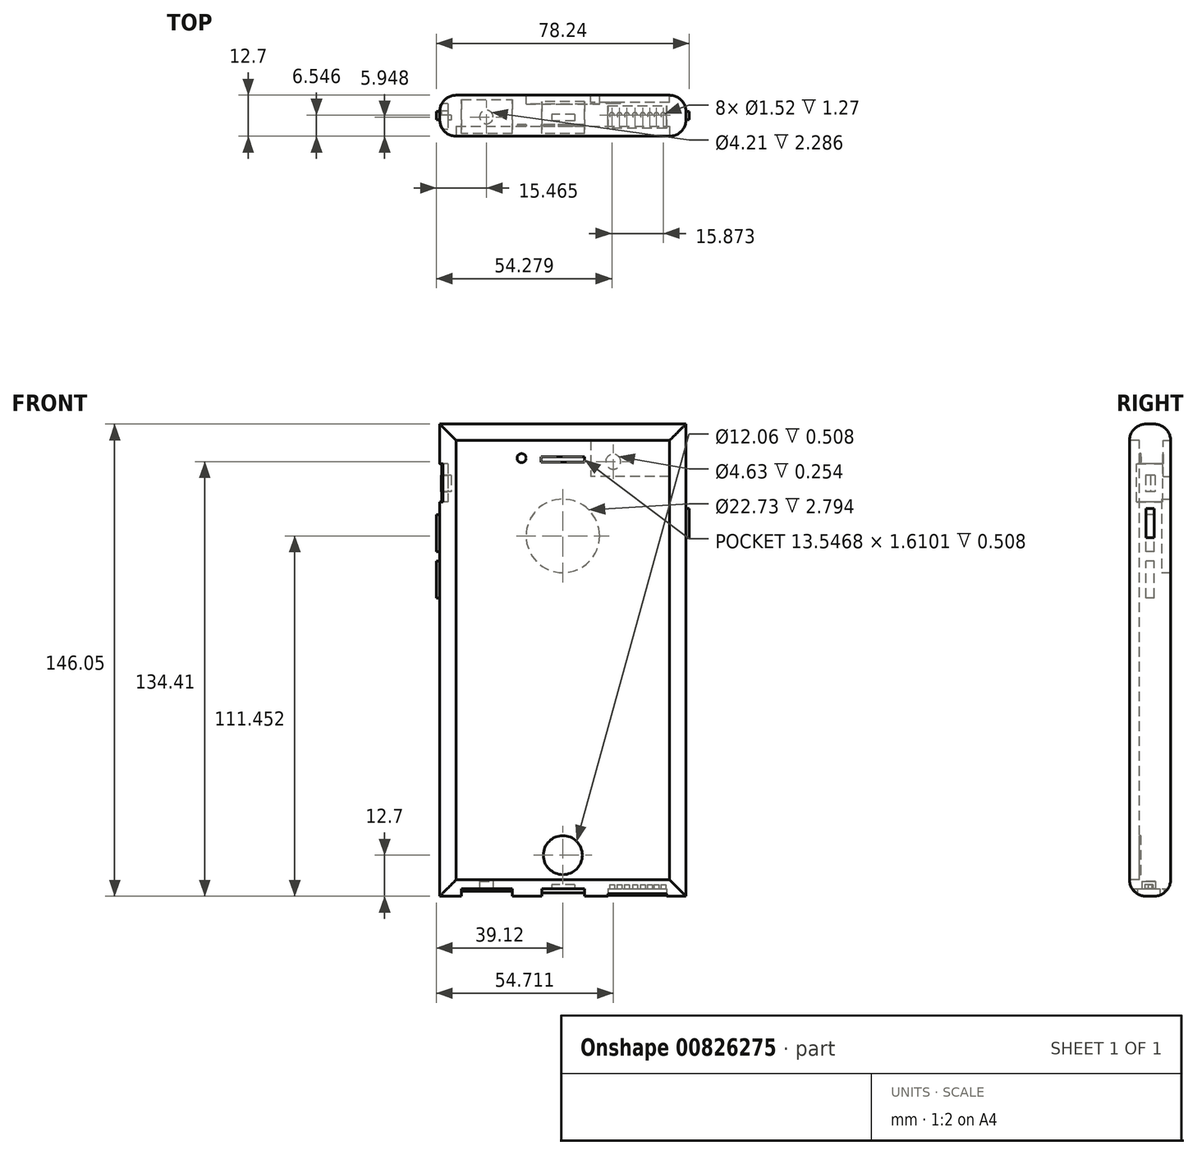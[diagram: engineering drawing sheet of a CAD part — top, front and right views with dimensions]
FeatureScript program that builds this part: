
annotation { "Feature Type Name" : "Feature", "Feature Type Description" : "" }
export const myFeature = defineFeature(function(context is Context, id is Id, definition is map)
    precondition{}
    {
        {
            var Q0;
            Q0=qCreatedBy(makeId("Front.planeOp"),FACE);
            var sketch = newSketch(context, id + "F0", { "sketchPlane" : qUnion([Q0])});
            skLineSegment(sketch, "E0.bottom", {"start": v(0, 0) * mm, "end": v(76.2, 0) * mm});
            skLineSegment(sketch, "E0.top", {"start": v(0, 146.05) * mm, "end": v(76.2, 146.05) * mm});
            skLineSegment(sketch, "E0.left", {"start": v(0, 0) * mm, "end": v(0, 146.05) * mm});
            skLineSegment(sketch, "E0.right", {"start": v(76.2, 0) * mm, "end": v(76.2, 146.05) * mm});
            skSolve(sketch);
        }
        {
            var Q0;
            Q0=makeQuery(id+"F0.imprint","IMPRINT",FACE,{"disambiguationData":[TD([[makeQuery(id+"F0.imprint","IMPRINT",EDGE,{"derivedFrom":sQuery(id+"F0.wireOp",EDGE,"E0.bottom")}),1.0]])]});
            extrude(context, id + "F1", {"entities" : qUnion([Q0]), "depth" : 12.7 * mm, "offsetDistance" : 25.4 * mm});
        }
        {
            var Q0;
            Q0=makeQuery(id+"F1.opExtrude","CAP_FACE",FACE,{"disambiguationData":[OSD([sQuery(id+"F0.wireOp",EDGE,"E0.bottom"),sQuery(id+"F0.wireOp",EDGE,"E0.top"),sQuery(id+"F0.wireOp",EDGE,"E0.left"),sQuery(id+"F0.wireOp",EDGE,"E0.right")])],"isStart":false});
            fillet(context, id + "F2", {"entities" : qUnion([Q0]), "radius" : 5.08 * mm, "tangentPropagation" : true, "allowEdgeOverflow" : false});
        }
        {
            var Q0;
            Q0=makeQuery(id+"F1.opExtrude","CAP_FACE",FACE,{"disambiguationData":[OSD([sQuery(id+"F0.wireOp",EDGE,"E0.bottom"),sQuery(id+"F0.wireOp",EDGE,"E0.top"),sQuery(id+"F0.wireOp",EDGE,"E0.left"),sQuery(id+"F0.wireOp",EDGE,"E0.right")])],"isStart":true});
            fillet(context, id + "F3", {"entities" : qUnion([Q0]), "radius" : 5.08 * mm, "tangentPropagation" : true, "allowEdgeOverflow" : false});
        }
        {
            var Q0;
            Q0=makeQuery(id+"F1.opExtrude","CAP_FACE",FACE,{"disambiguationData":[OSD([sQuery(id+"F0.wireOp",EDGE,"E0.bottom"),sQuery(id+"F0.wireOp",EDGE,"E0.top"),sQuery(id+"F0.wireOp",EDGE,"E0.left"),sQuery(id+"F0.wireOp",EDGE,"E0.right")])],"isStart":false});
            extrude(context, id + "F4", {"entities" : qUnion([Q0]), "operationType" : NewBodyOperationType.REMOVE, "oppositeDirection" : true, "depth" : 2.54 * mm, "offsetDistance" : 25.4 * mm});
        }
        {
            var Q0;
            Q0=makeQuery(id+"F1.opExtrude","SWEPT_FACE",FACE,{"disambiguationData":[OSD([sQuery(id+"F0.wireOp",EDGE,"E0.left")])]});
            var sketch = newSketch(context, id + "F5", { "sketchPlane" : qUnion([Q0])});
            skLineSegment(sketch, "E1.bottom", {"start": v(2.58, 133.75) * mm, "end": v(10.56, 133.75) * mm});
            skLineSegment(sketch, "E1.top", {"start": v(2.58, 122) * mm, "end": v(10.56, 122) * mm});
            skLineSegment(sketch, "E1.left", {"start": v(2.58, 133.75) * mm, "end": v(2.58, 122) * mm});
            skLineSegment(sketch, "E1.right", {"start": v(10.56, 133.75) * mm, "end": v(10.56, 122) * mm});
            skSolve(sketch);
        }
        {
            var Q0;
            {var subQ0=sQuery(id+"F5.wireOp",EDGE,"E1.left");Q0=makeQuery(id+"F5.imprint","IMPRINT",FACE,{"disambiguationData":[TD([[makeQuery(id+"F5.imprint","IMPRINT",EDGE,{"derivedFrom":subQ0}),1.0]])]});}
            var Q1;
            {var subQ0=sQuery(id+"F5.wireOp",EDGE,"E1.bottom");var subQ1=sQuery(id+"F0.wireOp",EDGE,"E0.left");var subQ2=makeQuery(id+"F1.opExtrude","SWEPT_FACE",FACE,{"disambiguationData":[OSD([subQ1])]});var subQ3=makeQuery(id+"F3.opFillet","BLEND_EDGE",EDGE,{"blendedFrom":[makeQuery(id+"F1.opExtrude","CAP_EDGE",EDGE,{"disambiguationData":[OSD([subQ1])],"isStart":true}),subQ2],"blendedInto":[subQ2]});var subQ4=makeQuery(id+"F5.imprint","INTERSECT",VERTEX,{"derivedFrom":[subQ3,subQ0]});Q1=makeQuery(id+"F5.imprint","IMPRINT",FACE,{"disambiguationData":[TD([[makeQuery(id+"F5.imprint","IMPRINT",EDGE,{"disambiguationData":[TD([[subQ4,-1.0]])],"derivedFrom":subQ0}),-1.0]])]});}
            var Q2;
            {var subQ0=sQuery(id+"F5.wireOp",EDGE,"E1.right");Q2=makeQuery(id+"F5.imprint","IMPRINT",FACE,{"disambiguationData":[TD([[makeQuery(id+"F5.imprint","IMPRINT",EDGE,{"derivedFrom":subQ0}),-1.0]])]});}
            extrude(context, id + "F6", {"entities" : qUnion([Q0, Q1, Q2]), "operationType" : NewBodyOperationType.REMOVE, "oppositeDirection" : true, "depth" : 2.54 * mm, "offsetDistance" : 25.4 * mm});
        }
        {
            var Q0;
            Q0=makeQuery(id+"F6.boolean.opBoolean","COPY",FACE,{"derivedFrom":makeQuery(id+"F6.opExtrude","CAP_FACE",FACE,{"disambiguationData":[OSD([sQuery(id+"F5.wireOp",EDGE,"E1.bottom"),sQuery(id+"F5.wireOp",EDGE,"E1.top"),sQuery(id+"F5.wireOp",EDGE,"E1.left"),sQuery(id+"F5.wireOp",EDGE,"E1.right")])],"isStart":false})});
            var sketch = newSketch(context, id + "F7", { "sketchPlane" : qUnion([Q0])});
            skLineSegment(sketch, "E2.bottom", {"start": v(4.8, 130.2) * mm, "end": v(7.68, 130.2) * mm});
            skLineSegment(sketch, "E2.top", {"start": v(4.8, 125.1) * mm, "end": v(7.68, 125.1) * mm});
            skLineSegment(sketch, "E2.left", {"start": v(4.8, 130.2) * mm, "end": v(4.8, 125.1) * mm});
            skLineSegment(sketch, "E2.right", {"start": v(7.68, 130.2) * mm, "end": v(7.68, 125.1) * mm});
            skSolve(sketch);
        }
        {
            var Q0;
            Q0=qSketchRegion(id+"F7",true);
            extrude(context, id + "F8", {"entities" : qUnion([Q0]), "operationType" : NewBodyOperationType.ADD, "depth" : 2.03 * mm, "offsetDistance" : 25.4 * mm});
        }
        {
            var Q0;
            Q0=makeQuery(id+"F8.opExtrude","CAP_FACE",FACE,{"disambiguationData":[OSD([sQuery(id+"F7.wireOp",EDGE,"E2.bottom"),sQuery(id+"F7.wireOp",EDGE,"E2.top"),sQuery(id+"F7.wireOp",EDGE,"E2.left"),sQuery(id+"F7.wireOp",EDGE,"E2.right")])],"isStart":false});
            var sketch = newSketch(context, id + "F9", { "sketchPlane" : qUnion([Q0])});
            skLineSegment(sketch, "E3", {"start": v(7.68, 125.1) * mm, "end": v(7.68, 130.2) * mm});
            skLineSegment(sketch, "E4", {"start": v(7.68, 130.2) * mm, "end": v(6.24, 130.2) * mm});
            skLineSegment(sketch, "E5", {"start": v(6.24, 130.2) * mm, "end": v(6.24, 125.1) * mm});
            skLineSegment(sketch, "E6", {"start": v(6.24, 125.1) * mm, "end": v(7.68, 125.1) * mm});
            skSolve(sketch);
        }
        {
            var Q0;
            Q0=makeQuery(id+"F9.imprint","IMPRINT",FACE,{"disambiguationData":[TD([[makeQuery(id+"F9.imprint","IMPRINT",EDGE,{"derivedFrom":sQuery(id+"F9.wireOp",EDGE,"E3")}),-1.0]])]});
            extrude(context, id + "F10", {"entities" : qUnion([Q0]), "operationType" : NewBodyOperationType.REMOVE, "oppositeDirection" : true, "depth" : 3.05 * mm, "offsetDistance" : 25.4 * mm});
        }
        {
            var Q0;
            {var subQ0=sQuery(id+"F0.wireOp",EDGE,"E0.bottom");var subQ1=sQuery(id+"F0.wireOp",EDGE,"E0.left");Q0=makeQuery(id+"F6.boolean.opBoolean","SPLIT",FACE,{"disambiguationData":[TD([makeQuery(id+"F1.opExtrude","SWEPT_FACE",FACE,{"disambiguationData":[OSD([subQ0])]})])],"derivedFrom":makeQuery(id+"F1.opExtrude","SWEPT_FACE",FACE,{"disambiguationData":[OSD([subQ1])]})});}
            var sketch = newSketch(context, id + "F11", { "sketchPlane" : qUnion([Q0])});
            skLineSegment(sketch, "E7.bottom", {"start": v(5.08, 118.03) * mm, "end": v(7.62, 118.03) * mm});
            skLineSegment(sketch, "E7.top", {"start": v(5.08, 106.6) * mm, "end": v(7.62, 106.6) * mm});
            skLineSegment(sketch, "E7.left", {"start": v(5.08, 118.03) * mm, "end": v(5.08, 106.6) * mm});
            skLineSegment(sketch, "E7.right", {"start": v(7.62, 118.03) * mm, "end": v(7.62, 106.6) * mm});
            skSolve(sketch);
        }
        {
            var Q0;
            Q0=makeQuery(id+"F11.imprint","IMPRINT",FACE,{"disambiguationData":[TD([[makeQuery(id+"F11.imprint","IMPRINT",EDGE,{"derivedFrom":sQuery(id+"F11.wireOp",EDGE,"E7.bottom")}),-1.0]])]});
            extrude(context, id + "F12", {"entities" : qUnion([Q0]), "operationType" : NewBodyOperationType.ADD, "depth" : 1.02 * mm, "offsetDistance" : 25.4 * mm});
        }
        {
            var Q0;
            {var subQ0=sQuery(id+"F0.wireOp",EDGE,"E0.bottom");var subQ2=sQuery(id+"F0.wireOp",EDGE,"E0.left");var subQ5=makeQuery(id+"F1.opExtrude","SWEPT_FACE",FACE,{"disambiguationData":[OSD([subQ0])]});Q0=makeQuery(id+"F12.boolean.opBoolean","SPLIT",FACE,{"disambiguationData":[TD([subQ5])],"derivedFrom":makeQuery(id+"F6.boolean.opBoolean","SPLIT",FACE,{"disambiguationData":[TD([subQ5])],"derivedFrom":makeQuery(id+"F1.opExtrude","SWEPT_FACE",FACE,{"disambiguationData":[OSD([subQ2])]})})});}
            var sketch = newSketch(context, id + "F13", { "sketchPlane" : qUnion([Q0])});
            skLineSegment(sketch, "E8.bottom", {"start": v(5.08, 103.7) * mm, "end": v(7.62, 103.7) * mm});
            skLineSegment(sketch, "E8.top", {"start": v(5.08, 92.27) * mm, "end": v(7.62, 92.27) * mm});
            skLineSegment(sketch, "E8.left", {"start": v(5.08, 103.7) * mm, "end": v(5.08, 92.27) * mm});
            skLineSegment(sketch, "E8.right", {"start": v(7.62, 103.7) * mm, "end": v(7.62, 92.27) * mm});
            skSolve(sketch);
        }
        {
            var Q0;
            Q0=makeQuery(id+"F13.imprint","IMPRINT",FACE,{"disambiguationData":[TD([[makeQuery(id+"F13.imprint","IMPRINT",EDGE,{"derivedFrom":sQuery(id+"F13.wireOp",EDGE,"E8.bottom")}),-1.0]])]});
            extrude(context, id + "F14", {"entities" : qUnion([Q0]), "operationType" : NewBodyOperationType.ADD, "depth" : 1.02 * mm, "offsetDistance" : 25.4 * mm});
        }
        {
            var Q0;
            Q0=makeQuery(id+"F4.boolean.opBoolean","COPY",FACE,{"derivedFrom":makeQuery(id+"F4.opExtrude","CAP_FACE",FACE,{"disambiguationData":[OSD([sQuery(id+"F0.wireOp",EDGE,"E0.bottom"),sQuery(id+"F0.wireOp",EDGE,"E0.top"),sQuery(id+"F0.wireOp",EDGE,"E0.left"),sQuery(id+"F0.wireOp",EDGE,"E0.right")])],"isStart":false})});
            var sketch = newSketch(context, id + "F15", { "sketchPlane" : qUnion([Q0])});
            skLineSegment(sketch, "E9", {"start": v(5.08, 5.08) * mm, "end": v(38.1, 5.08) * mm});
            skLineSegment(sketch, "E10", {"start": v(38.1, 5.08) * mm, "end": v(38.1, 12.7) * mm});
            skCircle(sketch, "E11", {"center": v(38.1, 12.7) * mm, "radius": 6.03 * mm});
            skSolve(sketch);
        }
        {
            var Q0;
            Q0=makeQuery(id+"F15.imprint","IMPRINT",FACE,{"disambiguationData":[TD([[makeQuery(id+"F15.imprint","IMPRINT",EDGE,{"derivedFrom":sQuery(id+"F15.wireOp",EDGE,"E11")}),1.0]])]});
            extrude(context, id + "F16", {"entities" : qUnion([Q0]), "operationType" : NewBodyOperationType.REMOVE, "oppositeDirection" : true, "depth" : 0.5 * mm, "offsetDistance" : 25.4 * mm});
        }
        {
            var Q0;
            Q0=makeQuery(id+"F1.opExtrude","SWEPT_FACE",FACE,{"disambiguationData":[OSD([sQuery(id+"F0.wireOp",EDGE,"E0.bottom")])]});
            var sketch = newSketch(context, id + "F17", { "sketchPlane" : qUnion([Q0])});
            skLineSegment(sketch, "E12.bottom", {"start": v(6.77, 11.85) * mm, "end": v(22.5, 11.85) * mm});
            skLineSegment(sketch, "E12.top", {"start": v(6.77, 1.38) * mm, "end": v(22.5, 1.38) * mm});
            skLineSegment(sketch, "E12.left", {"start": v(6.77, 11.85) * mm, "end": v(6.77, 1.38) * mm});
            skLineSegment(sketch, "E12.right", {"start": v(22.5, 11.85) * mm, "end": v(22.5, 1.38) * mm});
            skSolve(sketch);
        }
        {
            var Q0;
            Q0=qSketchRegion(id+"F17",true);
            var Q1;
            {var subQ0=sQuery(id+"F17.wireOp",EDGE,"E12.bottom");Q1=makeQuery(id+"F17.imprint","IMPRINT",FACE,{"disambiguationData":[TD([[makeQuery(id+"F17.imprint","IMPRINT",EDGE,{"derivedFrom":subQ0}),-1.0]])]});}
            extrude(context, id + "F18", {"entities" : qUnion([Q0, Q1]), "operationType" : NewBodyOperationType.REMOVE, "oppositeDirection" : true, "depth" : 2.3 * mm, "offsetDistance" : 25.4 * mm});
        }
        {
            var Q0;
            {var subQ0=sQuery(id+"F0.wireOp",EDGE,"E0.bottom");var subQ2=sQuery(id+"F0.wireOp",EDGE,"E0.right");var subQ5=makeQuery(id+"F1.opExtrude","SWEPT_FACE",FACE,{"disambiguationData":[OSD([subQ2])]});Q0=makeQuery(id+"FUvdi6jXHZb6WJ3_1.boolean.opBoolean","SPLIT",FACE,{"disambiguationData":[TD([subQ5])],"derivedFrom":makeQuery(id+"F18.boolean.opBoolean","SPLIT",FACE,{"disambiguationData":[TD([subQ5])],"derivedFrom":makeQuery(id+"F1.opExtrude","SWEPT_FACE",FACE,{"disambiguationData":[OSD([subQ0])]})})});}
            var sketch = newSketch(context, id + "F19", { "sketchPlane" : qUnion([Q0])});
            skLineSegment(sketch, "E13.bottom", {"start": v(52.05, 10.24) * mm, "end": v(70.18, 10.24) * mm});
            skLineSegment(sketch, "E13.top", {"start": v(52.05, 3.29) * mm, "end": v(70.18, 3.29) * mm});
            skLineSegment(sketch, "E13.left", {"start": v(52.05, 10.24) * mm, "end": v(52.05, 3.29) * mm});
            skLineSegment(sketch, "E13.right", {"start": v(70.18, 10.24) * mm, "end": v(70.18, 3.29) * mm});
            skSolve(sketch);
        }
        {
            var Q0;
            {var subQ0=sQuery(id+"F19.wireOp",EDGE,"E13.top");Q0=makeQuery(id+"F19.imprint","IMPRINT",FACE,{"disambiguationData":[TD([[makeQuery(id+"F19.imprint","IMPRINT",EDGE,{"derivedFrom":subQ0}),1.0]])]});}
            var Q1;
            {var subQ0=sQuery(id+"F19.wireOp",EDGE,"E13.left");var subQ1=sQuery(id+"F0.wireOp",EDGE,"E0.right");var subQ3=sQuery(id+"F0.wireOp",EDGE,"E0.bottom");var subQ5=makeQuery(id+"F1.opExtrude","SWEPT_FACE",FACE,{"disambiguationData":[OSD([subQ1])]});var subQ6=makeQuery(id+"F1.opExtrude","SWEPT_FACE",FACE,{"disambiguationData":[OSD([subQ3])]});var subQ9=makeQuery(id+"FUvdi6jXHZb6WJ3_1.boolean.opBoolean","SPLIT",EDGE,{"disambiguationData":[TD([subQ5])],"derivedFrom":makeQuery(id+"F18.boolean.opBoolean","SPLIT",EDGE,{"disambiguationData":[TD([subQ5])],"derivedFrom":makeQuery(id+"F2.opFillet","BLEND_EDGE",EDGE,{"blendedFrom":[makeQuery(id+"F1.opExtrude","CAP_EDGE",EDGE,{"disambiguationData":[OSD([subQ3])],"isStart":false}),subQ6],"blendedInto":[subQ6]})})});var subQ10=makeQuery(id+"F19.imprint","INTERSECT",VERTEX,{"derivedFrom":[subQ9,subQ0]});Q1=makeQuery(id+"F19.imprint","IMPRINT",FACE,{"disambiguationData":[TD([[makeQuery(id+"F19.imprint","IMPRINT",EDGE,{"disambiguationData":[TD([[subQ10,-1.0]])],"derivedFrom":subQ0}),1.0]])]});}
            var Q2;
            {var subQ0=sQuery(id+"F19.wireOp",EDGE,"E13.bottom");Q2=makeQuery(id+"F19.imprint","IMPRINT",FACE,{"disambiguationData":[TD([[makeQuery(id+"F19.imprint","IMPRINT",EDGE,{"derivedFrom":subQ0}),-1.0]])]});}
            extrude(context, id + "F20", {"entities" : qUnion([Q0, Q1, Q2]), "operationType" : NewBodyOperationType.REMOVE, "oppositeDirection" : true, "depth" : 2.3 * mm, "offsetDistance" : 25.4 * mm});
        }
        {
            var Q0;
            Q0=makeQuery(id+"F18.boolean.opBoolean","COPY",FACE,{"derivedFrom":makeQuery(id+"F18.opExtrude","CAP_FACE",FACE,{"disambiguationData":[OSD([sQuery(id+"F17.wireOp",EDGE,"E12.bottom"),sQuery(id+"F17.wireOp",EDGE,"E12.top"),sQuery(id+"F17.wireOp",EDGE,"E12.left"),sQuery(id+"F17.wireOp",EDGE,"E12.right")])],"isStart":false})});
            var sketch = newSketch(context, id + "F21", { "sketchPlane" : qUnion([Q0])});
            skCircle(sketch, "E14", {"center": v(14.44, 6.75) * mm, "radius": 2.1 * mm});
            skSolve(sketch);
        }
        {
            var Q0;
            Q0=qSketchRegion(id+"F21",true);
            extrude(context, id + "F22", {"entities" : qUnion([Q0]), "operationType" : NewBodyOperationType.REMOVE, "oppositeDirection" : true, "depth" : 2.3 * mm, "offsetDistance" : 25.4 * mm});
        }
        {
            var Q0;
            Q0=makeQuery(id+"F20.boolean.opBoolean","COPY",FACE,{"derivedFrom":makeQuery(id+"F20.opExtrude","CAP_FACE",FACE,{"disambiguationData":[OSD([sQuery(id+"F19.wireOp",EDGE,"E13.bottom"),sQuery(id+"F19.wireOp",EDGE,"E13.top"),sQuery(id+"F19.wireOp",EDGE,"E13.left"),sQuery(id+"F19.wireOp",EDGE,"E13.right")])],"isStart":false})});
            var sketch = newSketch(context, id + "F23", { "sketchPlane" : qUnion([Q0])});
            skLineSegment(sketch, "E15", {"start": v(52.05, 6.15) * mm, "end": v(70.18, 6.15) * mm});
            skCircle(sketch, "E16", {"center": v(53.26, 6.15) * mm, "radius": 0.76 * mm});
            skCircle(sketch, "E17", {"center": v(55.62, 6.15) * mm, "radius": 0.76 * mm});
            skCircle(sketch, "E18", {"center": v(57.9, 6.15) * mm, "radius": 0.76 * mm});
            skCircle(sketch, "E19", {"center": v(60.4, 6.15) * mm, "radius": 0.76 * mm});
            skCircle(sketch, "E20", {"center": v(62.83, 6.15) * mm, "radius": 0.76 * mm});
            skCircle(sketch, "E21", {"center": v(65.04, 6.15) * mm, "radius": 0.76 * mm});
            skCircle(sketch, "E22", {"center": v(67.06, 6.15) * mm, "radius": 0.76 * mm});
            skCircle(sketch, "E23", {"center": v(69.13, 6.15) * mm, "radius": 0.76 * mm});
            skSolve(sketch);
        }
        {
            var Q0;
            Q0=qSketchRegion(id+"F23",true);
            extrude(context, id + "F24", {"entities" : qUnion([Q0]), "operationType" : NewBodyOperationType.REMOVE, "oppositeDirection" : true, "depth" : 1.27 * mm, "offsetDistance" : 25.4 * mm});
        }
        {
            var Q0;
            Q0=makeQuery(id+"F16.boolean.opBoolean","COPY",FACE,{"derivedFrom":makeQuery(id+"F16.opExtrude","CAP_FACE",FACE,{"disambiguationData":[OSD([sQuery(id+"F15.wireOp",EDGE,"E11")])],"isStart":false})});
            var sketch = newSketch(context, id + "F25", { "sketchPlane" : qUnion([Q0])});
            skLineSegment(sketch, "E24.bottom", {"start": v(44.87, 135.88) * mm, "end": v(31.33, 135.88) * mm});
            skLineSegment(sketch, "E24.top", {"start": v(44.87, 134.27) * mm, "end": v(31.33, 134.27) * mm});
            skLineSegment(sketch, "E24.left", {"start": v(44.87, 135.88) * mm, "end": v(44.87, 134.27) * mm});
            skLineSegment(sketch, "E24.right", {"start": v(31.33, 135.88) * mm, "end": v(31.33, 134.27) * mm});
            skPoint(sketch, "E24.middle", {"position": v(38.1, 135.08) * mm});
            skSolve(sketch);
        }
        {
            var Q0;
            Q0=qSketchRegion(id+"F25",true);
            var Q1;
            Q1=makeQuery(id+"F4.boolean.opBoolean","COPY",FACE,{"derivedFrom":makeQuery(id+"F4.opExtrude","CAP_FACE",FACE,{"disambiguationData":[OSD([sQuery(id+"F0.wireOp",EDGE,"E0.bottom"),sQuery(id+"F0.wireOp",EDGE,"E0.top"),sQuery(id+"F0.wireOp",EDGE,"E0.left"),sQuery(id+"F0.wireOp",EDGE,"E0.right")])],"isStart":false})});
            extrude(context, id + "F26", {"entities" : qUnion([Q0, Q1]), "operationType" : NewBodyOperationType.REMOVE, "oppositeDirection" : true, "depth" : 0.5 * mm, "offsetDistance" : 25.4 * mm});
        }
        {
            var Q0;
            Q0=makeQuery(id+"F26.boolean.opBoolean","MERGE",FACE,{"derivedFrom":[makeQuery(id+"F16.boolean.opBoolean","COPY",FACE,{"derivedFrom":makeQuery(id+"F16.opExtrude","CAP_FACE",FACE,{"disambiguationData":[OSD([sQuery(id+"F15.wireOp",EDGE,"E11")])],"isStart":false})}),makeQuery(id+"F26.opExtrude","CAP_FACE",FACE,{"disambiguationData":[OSD([sQuery(id+"F0.wireOp",EDGE,"E0.bottom"),sQuery(id+"F0.wireOp",EDGE,"E0.top"),sQuery(id+"F0.wireOp",EDGE,"E0.left"),sQuery(id+"F0.wireOp",EDGE,"E0.right")])],"isStart":false})]});
            var sketch = newSketch(context, id + "F27", { "sketchPlane" : qUnion([Q0])});
            skCircle(sketch, "E25", {"center": v(25.32, 135.5) * mm, "radius": 1.4 * mm});
            skSolve(sketch);
        }
        {
            var Q0;
            Q0=makeQuery(id+"F27.imprint","IMPRINT",FACE,{"disambiguationData":[TD([[makeQuery(id+"F27.imprint","IMPRINT",EDGE,{"derivedFrom":sQuery(id+"F27.wireOp",EDGE,"E25")}),1.0]])]});
            extrude(context, id + "F28", {"entities" : qUnion([Q0]), "operationType" : NewBodyOperationType.REMOVE, "oppositeDirection" : true, "depth" : 0.5 * mm, "offsetDistance" : 25.4 * mm});
        }
        {
            var Q0;
            Q0=makeQuery(id+"F26.boolean.opBoolean","MERGE",FACE,{"derivedFrom":[makeQuery(id+"F16.boolean.opBoolean","COPY",FACE,{"derivedFrom":makeQuery(id+"F16.opExtrude","CAP_FACE",FACE,{"disambiguationData":[OSD([sQuery(id+"F15.wireOp",EDGE,"E11")])],"isStart":false})}),makeQuery(id+"F26.opExtrude","CAP_FACE",FACE,{"disambiguationData":[OSD([sQuery(id+"F0.wireOp",EDGE,"E0.bottom"),sQuery(id+"F0.wireOp",EDGE,"E0.top"),sQuery(id+"F0.wireOp",EDGE,"E0.left"),sQuery(id+"F0.wireOp",EDGE,"E0.right")])],"isStart":false})]});
            var sketch = newSketch(context, id + "F29", { "sketchPlane" : qUnion([Q0])});
            skLineSegment(sketch, "E26", {"start": v(38.1, 5.08) * mm, "end": v(38.1, 12.7) * mm});
            skCircle(sketch, "E27", {"center": v(38.1, 12.7) * mm, "radius": 6.03 * mm});
            skSolve(sketch);
        }
        {
            var Q0;
            Q0=makeQuery(id+"F29.imprint","IMPRINT",FACE,{"disambiguationData":[TD([[makeQuery(id+"F29.imprint","IMPRINT",EDGE,{"derivedFrom":sQuery(id+"F29.wireOp",EDGE,"E27")}),1.0]])]});
            extrude(context, id + "F30", {"entities" : qUnion([Q0]), "operationType" : NewBodyOperationType.REMOVE, "oppositeDirection" : true, "depth" : 0.5 * mm, "offsetDistance" : 25.4 * mm});
        }
        {
            var Q0;
            {var subQ0=sQuery(id+"F0.wireOp",EDGE,"E0.bottom");var subQ2=makeQuery(id+"F18.opExtrude","SWEPT_FACE",FACE,{"disambiguationData":[OSD([sQuery(id+"F17.wireOp",EDGE,"E12.right")])]});var subQ4=sQuery(id+"F0.wireOp",EDGE,"E0.right");Q0=makeQuery(id+"F20.boolean.opBoolean","SPLIT",FACE,{"disambiguationData":[TD([makeQuery(id+"F18.boolean.opBoolean","COPY",FACE,{"derivedFrom":subQ2})])],"derivedFrom":makeQuery(id+"F18.boolean.opBoolean","SPLIT",FACE,{"disambiguationData":[TD([makeQuery(id+"F1.opExtrude","SWEPT_FACE",FACE,{"disambiguationData":[OSD([subQ4])]})])],"derivedFrom":makeQuery(id+"F1.opExtrude","SWEPT_FACE",FACE,{"disambiguationData":[OSD([subQ0])]})})});}
            var sketch = newSketch(context, id + "F31", { "sketchPlane" : qUnion([Q0])});
            skLineSegment(sketch, "E28", {"start": v(38.23, 17.24) * mm, "end": v(38.23, 13.45) * mm});
            skLineSegment(sketch, "E29.bottom", {"start": v(38.23, 13.45) * mm, "end": v(31.63, 13.45) * mm});
            skLineSegment(sketch, "E29.top", {"start": v(38.23, 2.02) * mm, "end": v(31.63, 2.02) * mm});
            skLineSegment(sketch, "E29.left", {"start": v(38.23, 13.45) * mm, "end": v(38.23, 2.02) * mm});
            skLineSegment(sketch, "E29.right", {"start": v(31.63, 13.45) * mm, "end": v(31.63, 2.02) * mm});
            skLineSegment(sketch, "E30.bottom", {"start": v(38.23, 13.45) * mm, "end": v(44.84, 13.45) * mm});
            skLineSegment(sketch, "E30.top", {"start": v(38.23, 2.02) * mm, "end": v(44.84, 2.02) * mm});
            skLineSegment(sketch, "E30.right", {"start": v(44.84, 13.45) * mm, "end": v(44.84, 2.02) * mm});
            skSolve(sketch);
        }
        {
            var Q0;
            {var subQ0=sQuery(id+"F31.wireOp",EDGE,"E29.top");Q0=makeQuery(id+"F31.imprint","IMPRINT",FACE,{"disambiguationData":[TD([[makeQuery(id+"F31.imprint","IMPRINT",EDGE,{"derivedFrom":subQ0}),-1.0]])]});}
            var Q1;
            {var subQ0=sQuery(id+"F31.wireOp",EDGE,"E30.bottom");Q1=makeQuery(id+"F31.imprint","IMPRINT",FACE,{"disambiguationData":[TD([[makeQuery(id+"F31.imprint","IMPRINT",EDGE,{"derivedFrom":subQ0}),-1.0]])]});}
            var Q2;
            {var subQ0=sQuery(id+"F31.wireOp",EDGE,"E30.top");Q2=makeQuery(id+"F31.imprint","IMPRINT",FACE,{"disambiguationData":[TD([[makeQuery(id+"F31.imprint","IMPRINT",EDGE,{"derivedFrom":subQ0}),1.0]])]});}
            var Q3;
            {var subQ0=sQuery(id+"F31.wireOp",EDGE,"E29.right");var subQ1=sQuery(id+"F0.wireOp",EDGE,"E0.bottom");var subQ2=makeQuery(id+"F1.opExtrude","SWEPT_FACE",FACE,{"disambiguationData":[OSD([subQ1])]});var subQ4=makeQuery(id+"F18.opExtrude","SWEPT_FACE",FACE,{"disambiguationData":[OSD([sQuery(id+"F17.wireOp",EDGE,"E12.right")])]});var subQ5=makeQuery(id+"F18.boolean.opBoolean","COPY",FACE,{"derivedFrom":subQ4});var subQ7=sQuery(id+"F0.wireOp",EDGE,"E0.right");var subQ8=makeQuery(id+"F1.opExtrude","SWEPT_FACE",FACE,{"disambiguationData":[OSD([subQ7])]});var subQ9=makeQuery(id+"F20.boolean.opBoolean","SPLIT",EDGE,{"disambiguationData":[TD([subQ5])],"derivedFrom":makeQuery(id+"F18.boolean.opBoolean","SPLIT",EDGE,{"disambiguationData":[TD([subQ8])],"derivedFrom":makeQuery(id+"F2.opFillet","BLEND_EDGE",EDGE,{"blendedFrom":[makeQuery(id+"F1.opExtrude","CAP_EDGE",EDGE,{"disambiguationData":[OSD([subQ1])],"isStart":false}),subQ2],"blendedInto":[subQ2]})})});var subQ10=makeQuery(id+"F31.imprint","INTERSECT",VERTEX,{"derivedFrom":[subQ9,subQ0]});Q3=makeQuery(id+"F31.imprint","IMPRINT",FACE,{"disambiguationData":[TD([[makeQuery(id+"F31.imprint","IMPRINT",EDGE,{"disambiguationData":[TD([[subQ10,-1.0]])],"derivedFrom":subQ0}),1.0]])]});}
            var Q4;
            {var subQ0=sQuery(id+"F31.wireOp",EDGE,"E29.left");var subQ1=sQuery(id+"F0.wireOp",EDGE,"E0.bottom");var subQ2=makeQuery(id+"F1.opExtrude","SWEPT_FACE",FACE,{"disambiguationData":[OSD([subQ1])]});var subQ4=makeQuery(id+"F18.opExtrude","SWEPT_FACE",FACE,{"disambiguationData":[OSD([sQuery(id+"F17.wireOp",EDGE,"E12.right")])]});var subQ5=makeQuery(id+"F18.boolean.opBoolean","COPY",FACE,{"derivedFrom":subQ4});var subQ7=sQuery(id+"F0.wireOp",EDGE,"E0.right");var subQ8=makeQuery(id+"F1.opExtrude","SWEPT_FACE",FACE,{"disambiguationData":[OSD([subQ7])]});var subQ9=makeQuery(id+"F20.boolean.opBoolean","SPLIT",EDGE,{"disambiguationData":[TD([subQ5])],"derivedFrom":makeQuery(id+"F18.boolean.opBoolean","SPLIT",EDGE,{"disambiguationData":[TD([subQ8])],"derivedFrom":makeQuery(id+"F2.opFillet","BLEND_EDGE",EDGE,{"blendedFrom":[makeQuery(id+"F1.opExtrude","CAP_EDGE",EDGE,{"disambiguationData":[OSD([subQ1])],"isStart":false}),subQ2],"blendedInto":[subQ2]})})});var subQ10=makeQuery(id+"F31.imprint","INTERSECT",VERTEX,{"derivedFrom":[subQ9,subQ0]});Q4=makeQuery(id+"F31.imprint","IMPRINT",FACE,{"disambiguationData":[TD([[makeQuery(id+"F31.imprint","IMPRINT",EDGE,{"disambiguationData":[TD([[subQ10,-1.0]])],"derivedFrom":subQ0}),1.0]])]});}
            var Q5;
            {var subQ0=sQuery(id+"F31.wireOp",EDGE,"E29.bottom");Q5=makeQuery(id+"F31.imprint","IMPRINT",FACE,{"disambiguationData":[TD([[makeQuery(id+"F31.imprint","IMPRINT",EDGE,{"derivedFrom":subQ0}),1.0]])]});}
            extrude(context, id + "F32", {"entities" : qUnion([Q0, Q1, Q2, Q3, Q4, Q5]), "operationType" : NewBodyOperationType.REMOVE, "oppositeDirection" : true, "depth" : 2.3 * mm, "offsetDistance" : 25.4 * mm});
        }
        {
            var Q0;
            Q0=makeQuery(id+"F32.boolean.opBoolean","COPY",FACE,{"derivedFrom":makeQuery(id+"F32.opExtrude","CAP_FACE",FACE,{"disambiguationData":[OSD([sQuery(id+"F31.wireOp",EDGE,"E29.bottom"),sQuery(id+"F31.wireOp",EDGE,"E29.top"),sQuery(id+"F31.wireOp",EDGE,"E29.right"),sQuery(id+"F31.wireOp",EDGE,"E30.bottom"),sQuery(id+"F31.wireOp",EDGE,"E30.top"),sQuery(id+"F31.wireOp",EDGE,"E30.right")])],"isStart":false})});
            var sketch = newSketch(context, id + "F33", { "sketchPlane" : qUnion([Q0])});
            skLineSegment(sketch, "E31", {"start": v(31.63, 6.94) * mm, "end": v(38.23, 6.94) * mm});
            skPoint(sketch, "E31.endSnap0", {"position": v(44.84, 6.94) * mm});
            skLineSegment(sketch, "E32.bottom", {"start": v(41.81, 5.89) * mm, "end": v(34.65, 5.89) * mm});
            skLineSegment(sketch, "E32.top", {"start": v(41.81, 8) * mm, "end": v(34.65, 8) * mm});
            skLineSegment(sketch, "E32.left", {"start": v(41.81, 5.89) * mm, "end": v(41.81, 8) * mm});
            skLineSegment(sketch, "E32.right", {"start": v(34.65, 5.89) * mm, "end": v(34.65, 8) * mm});
            skPoint(sketch, "E32.middle", {"position": v(38.23, 6.94) * mm});
            skSolve(sketch);
        }
        {
            var Q0;
            {var subQ1=sQuery(id+"F33.wireOp",EDGE,"E32.bottom");Q0=makeQuery(id+"F33.imprint","IMPRINT",FACE,{"disambiguationData":[TD([[makeQuery(id+"F33.imprint","IMPRINT",EDGE,{"derivedFrom":subQ1}),-1.0]])]});}
            extrude(context, id + "F34", {"entities" : qUnion([Q0]), "operationType" : NewBodyOperationType.REMOVE, "oppositeDirection" : true, "depth" : 1.27 * mm, "offsetDistance" : 25.4 * mm});
        }
        {
            var Q0;
            Q0=makeQuery(id+"F1.opExtrude","CAP_FACE",FACE,{"disambiguationData":[OSD([sQuery(id+"F0.wireOp",EDGE,"E0.bottom"),sQuery(id+"F0.wireOp",EDGE,"E0.top"),sQuery(id+"F0.wireOp",EDGE,"E0.left"),sQuery(id+"F0.wireOp",EDGE,"E0.right")])],"isStart":true});
            var sketch = newSketch(context, id + "F35", { "sketchPlane" : qUnion([Q0])});
            skLineSegment(sketch, "E33.bottom", {"start": v(-71.12, 140.97) * mm, "end": v(-46.68, 140.97) * mm});
            skLineSegment(sketch, "E33.top", {"start": v(-71.12, 129.76) * mm, "end": v(-46.68, 129.76) * mm});
            skLineSegment(sketch, "E33.left", {"start": v(-71.12, 140.97) * mm, "end": v(-71.12, 129.76) * mm});
            skLineSegment(sketch, "E33.right", {"start": v(-46.68, 140.97) * mm, "end": v(-46.68, 129.76) * mm});
            skSolve(sketch);
        }
        {
            var Q0;
            Q0=makeQuery(id+"F35.imprint","IMPRINT",FACE,{"disambiguationData":[TD([[makeQuery(id+"F35.imprint","IMPRINT",EDGE,{"derivedFrom":sQuery(id+"F35.wireOp",EDGE,"E33.bottom")}),1.0]])]});
            extrude(context, id + "F36", {"entities" : qUnion([Q0]), "operationType" : NewBodyOperationType.REMOVE, "oppositeDirection" : true, "depth" : 2.3 * mm, "offsetDistance" : 25.4 * mm});
        }
        {
            var Q0;
            Q0=makeQuery(id+"F36.boolean.opBoolean","COPY",FACE,{"derivedFrom":makeQuery(id+"F36.opExtrude","CAP_FACE",FACE,{"disambiguationData":[OSD([sQuery(id+"F35.wireOp",EDGE,"E33.bottom"),sQuery(id+"F35.wireOp",EDGE,"E33.top"),sQuery(id+"F35.wireOp",EDGE,"E33.left"),sQuery(id+"F35.wireOp",EDGE,"E33.right")])],"isStart":false})});
            var sketch = newSketch(context, id + "F37", { "sketchPlane" : qUnion([Q0])});
            skCircle(sketch, "E34", {"center": v(-64.77, 134.85) * mm, "radius": 3.81 * mm});
            skCircle(sketch, "E35", {"center": v(-53.7, 134.85) * mm, "radius": 2.82 * mm});
            skSolve(sketch);
        }
        {
            var Q0;
            Q0=sQuery(id+"F37.wireOp",EDGE,"E34");
            extrude(context, id + "F38", {"bodyType" : ToolBodyType.SURFACE, "surfaceEntities" : qUnion([Q0]), "depth" : 1.02 * mm, "offsetDistance" : 25.4 * mm});
        }
        {
            var Q0;
            Q0=makeQuery(id+"F36.boolean.opBoolean","COPY",FACE,{"derivedFrom":makeQuery(id+"F36.opExtrude","CAP_FACE",FACE,{"disambiguationData":[OSD([sQuery(id+"F35.wireOp",EDGE,"E33.bottom"),sQuery(id+"F35.wireOp",EDGE,"E33.top"),sQuery(id+"F35.wireOp",EDGE,"E33.left"),sQuery(id+"F35.wireOp",EDGE,"E33.right")])],"isStart":false})});
            var sketch = newSketch(context, id + "F39", { "sketchPlane" : qUnion([Q0])});
            skCircle(sketch, "E36", {"center": v(-53.7, 134.41) * mm, "radius": 2.31 * mm});
            skSolve(sketch);
        }
        {
            var Q0;
            Q0=makeQuery(id+"F39.imprint","IMPRINT",FACE,{"disambiguationData":[TD([[makeQuery(id+"F39.imprint","IMPRINT",EDGE,{"derivedFrom":sQuery(id+"F39.wireOp",EDGE,"E36")}),1.0]])]});
            extrude(context, id + "F40", {"entities" : qUnion([Q0]), "operationType" : NewBodyOperationType.REMOVE, "oppositeDirection" : true, "depth" : 0.25 * mm, "offsetDistance" : 25.4 * mm});
        }
        {
            var Q0;
            Q0=makeQuery(id+"F1.opExtrude","CAP_FACE",FACE,{"disambiguationData":[OSD([sQuery(id+"F0.wireOp",EDGE,"E0.bottom"),sQuery(id+"F0.wireOp",EDGE,"E0.top"),sQuery(id+"F0.wireOp",EDGE,"E0.left"),sQuery(id+"F0.wireOp",EDGE,"E0.right")])],"isStart":true});
            var sketch = newSketch(context, id + "F41", { "sketchPlane" : qUnion([Q0])});
            skLineSegment(sketch, "E37", {"start": v(-5.08, 140.97) * mm, "end": v(-38.1, 140.97) * mm});
            skLineSegment(sketch, "E38", {"start": v(-38.1, 140.97) * mm, "end": v(-38.1, 111.45) * mm});
            skCircle(sketch, "E39", {"center": v(-38.1, 111.45) * mm, "radius": 11.36 * mm});
            skSolve(sketch);
        }
        {
            var Q0;
            Q0=qSketchRegion(id+"F41",true);
            var Q1;
            Q1=makeQuery(id+"F41.imprint","IMPRINT",FACE,{"disambiguationData":[TD([[makeQuery(id+"F41.imprint","IMPRINT",EDGE,{"derivedFrom":sQuery(id+"F41.wireOp",EDGE,"E39")}),1.0]])]});
            extrude(context, id + "F42", {"entities" : qUnion([Q0, Q1]), "operationType" : NewBodyOperationType.REMOVE, "oppositeDirection" : true, "depth" : 1.02 * mm, "offsetDistance" : 25.4 * mm});
        }
        {
            var Q0;
            Q0=makeQuery(id+"F42.boolean.opBoolean","COPY",FACE,{"derivedFrom":makeQuery(id+"F42.opExtrude","CAP_FACE",FACE,{"disambiguationData":[OSD([sQuery(id+"F41.wireOp",EDGE,"E39")])],"isStart":false})});
            extrude(context, id + "F43", {"entities" : qUnion([Q0]), "operationType" : NewBodyOperationType.REMOVE, "oppositeDirection" : true, "depth" : 1.78 * mm, "offsetDistance" : 25.4 * mm});
        }
        {
            var Q0;
            Q0=makeQuery(id+"F1.opExtrude","SWEPT_FACE",FACE,{"disambiguationData":[OSD([sQuery(id+"F0.wireOp",EDGE,"E0.right")])]});
            var sketch = newSketch(context, id + "F44", { "sketchPlane" : qUnion([Q0])});
            skLineSegment(sketch, "E40.bottom", {"start": v(-5.08, 119.84) * mm, "end": v(-7.62, 119.84) * mm});
            skLineSegment(sketch, "E40.top", {"start": v(-5.08, 110.9) * mm, "end": v(-7.62, 110.9) * mm});
            skLineSegment(sketch, "E40.left", {"start": v(-5.08, 119.84) * mm, "end": v(-5.08, 110.9) * mm});
            skLineSegment(sketch, "E40.right", {"start": v(-7.62, 119.84) * mm, "end": v(-7.62, 110.9) * mm});
            skSolve(sketch);
        }
        {
            var Q0;
            Q0=makeQuery(id+"F44.imprint","IMPRINT",FACE,{"disambiguationData":[TD([[makeQuery(id+"F44.imprint","IMPRINT",EDGE,{"derivedFrom":sQuery(id+"F44.wireOp",EDGE,"E40.bottom")}),1.0]])]});
            extrude(context, id + "F45", {"entities" : qUnion([Q0]), "operationType" : NewBodyOperationType.ADD, "depth" : 1.02 * mm, "offsetDistance" : 25.4 * mm});
        }
    });
